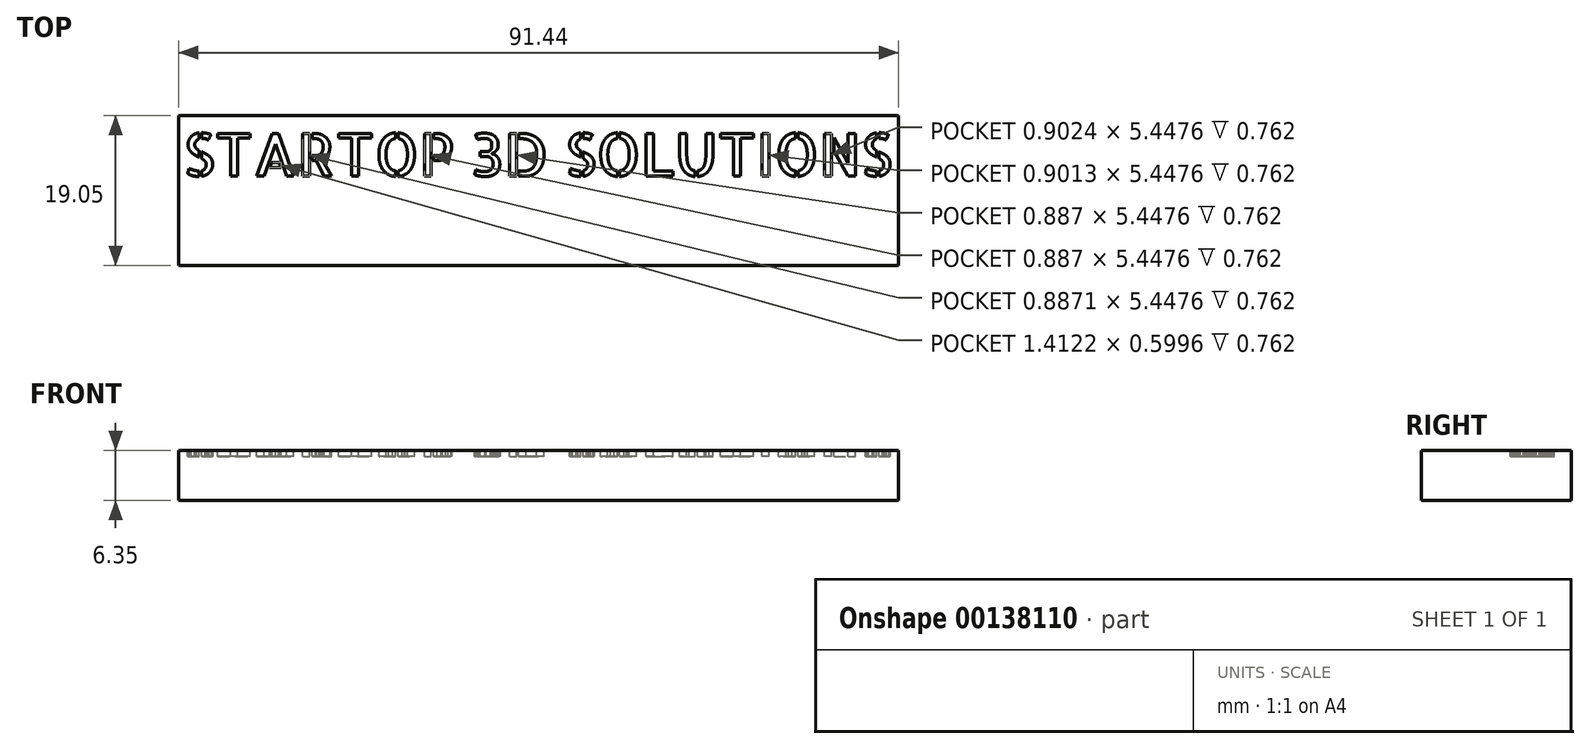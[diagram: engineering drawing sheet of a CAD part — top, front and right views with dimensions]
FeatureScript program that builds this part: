
annotation { "Feature Type Name" : "Feature", "Feature Type Description" : "" }
export const myFeature = defineFeature(function(context is Context, id is Id, definition is map)
    precondition{}
    {
        {
            var Q0;
            Q0=qCreatedBy(makeId("Top.planeOp"),FACE);
            var sketch = newSketch(context, id + "F0", { "sketchPlane" : qUnion([Q0])});
            skLineSegment(sketch, "E0.bottom", {"start": v(0, 0) * mm, "end": v(91.44, 0) * mm});
            skLineSegment(sketch, "E0.top", {"start": v(0, 19.05) * mm, "end": v(91.44, 19.05) * mm});
            skLineSegment(sketch, "E0.left", {"start": v(0, 0) * mm, "end": v(0, 19.05) * mm});
            skLineSegment(sketch, "E0.right", {"start": v(91.44, 0) * mm, "end": v(91.44, 19.05) * mm});
            skSolve(sketch);
        }
        {
            var Q0;
            Q0 = qSketchRegion(id + "F0", true);
            extrude(context, id + "F1", {"entities" : qUnion([Q0]), "depth" : 6.35 * mm});
        }
        {
            var Q0;
            Q0=makeQuery(id+"F1.opExtrude","CAP_FACE",FACE,{"disambiguationData":[OSD([sQuery(id+"F0.wireOp",EDGE,"E0.bottom"),sQuery(id+"F0.wireOp",EDGE,"E0.top"),sQuery(id+"F0.wireOp",EDGE,"E0.left"),sQuery(id+"F0.wireOp",EDGE,"E0.right")])],"isStart":false});
            var sketch = newSketch(context, id + "F2", { "sketchPlane" : qUnion([Q0])});
            skLineSegment(sketch, "E1", {"start": v(0, 9.53) * mm, "end": v(91.44, 9.53) * mm, "construction": true});
            skText(sketch, "E2", { "text": "STARTOP 3D SOLUTIONS", "fontName": "AllertaStencil-Regular.ttf"});
            const initialGuessF2  = {"E2": [0.00056, 0.01133, 1, 0, 0.00545]};
            skSetInitialGuess(sketch, initialGuessF2);
            skSolve(sketch);
        }
        {
            var Q0;
            Q0 = qSketchRegion(id + "F2", true);
            extrude(context, id + "F3", {"entities" : qUnion([Q0]), "operationType" : NewBodyOperationType.REMOVE, "oppositeDirection" : true, "depth" : 0.76 * mm});
        }
    });
